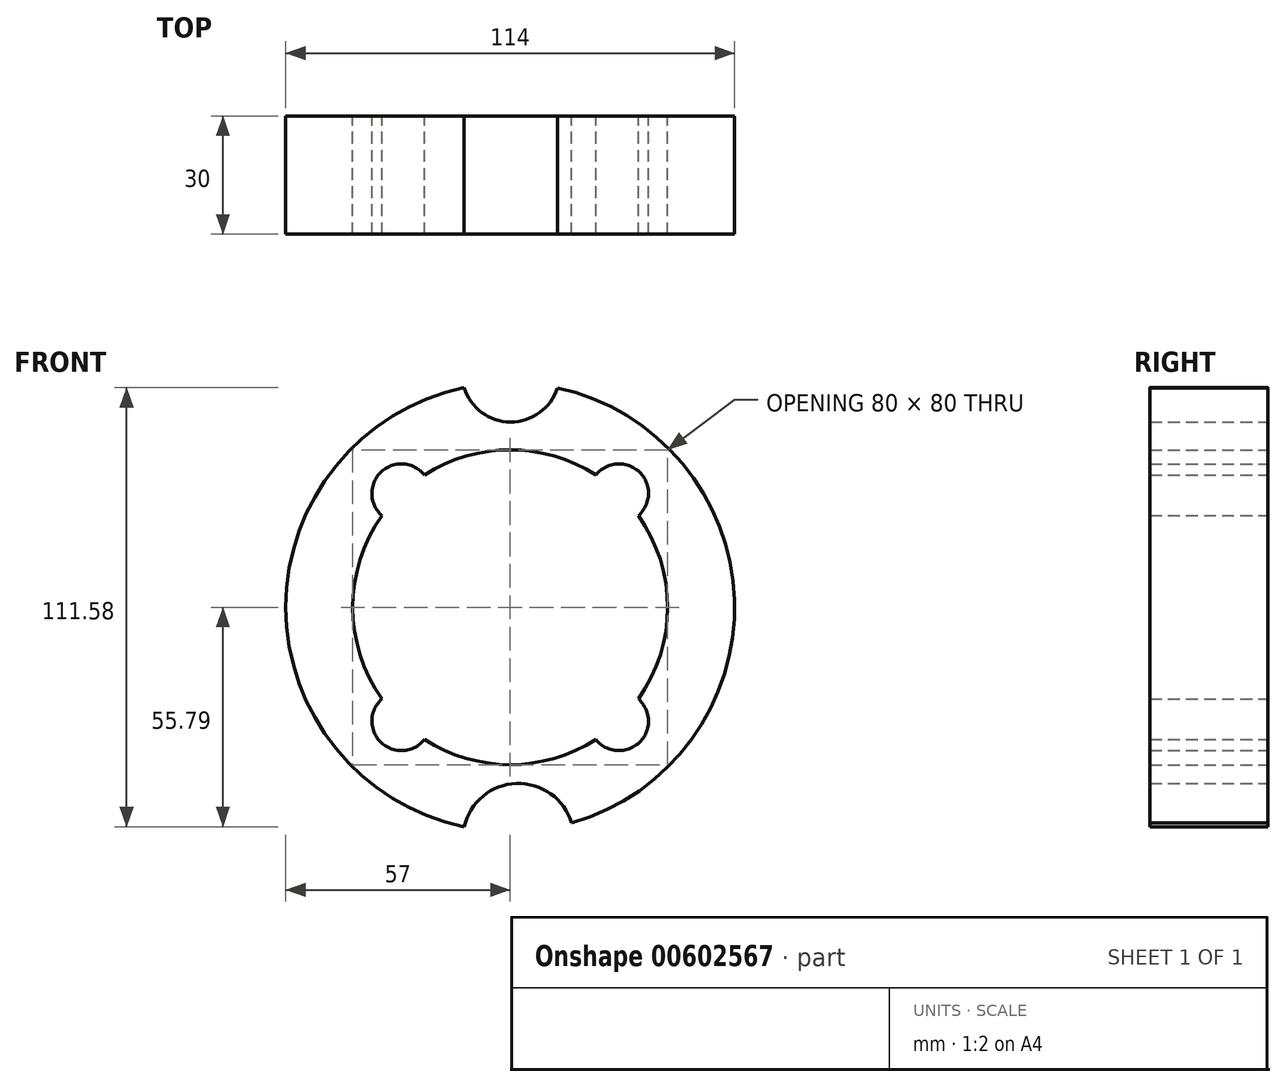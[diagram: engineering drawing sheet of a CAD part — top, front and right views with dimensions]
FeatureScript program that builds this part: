
annotation { "Feature Type Name" : "Feature", "Feature Type Description" : "" }
export const myFeature = defineFeature(function(context is Context, id is Id, definition is map)
    precondition{}
    {
        {
            var Q0;
            Q0=qCreatedBy(makeId("Front.planeOp"),FACE);
            var sketch = newSketch(context, id + "F0", { "sketchPlane" : qUnion([Q0])});
            skArc(sketch, "E0", {"start": v(-11.7, 55.79) * mm, "mid": v(-57, 0) * mm, "end": v(-11.7, -55.79) * mm});
            skCircle(sketch, "E1", {"center": v(0, 0) * mm, "radius": 13 * mm});
            skCircle(sketch, "E2", {"center": v(0, 0) * mm, "radius": 40 * mm});
            skCircle(sketch, "E3", {"center": v(0, 0) * mm, "radius": 25 * mm});
            skArc(sketch, "E4", {"start": v(-11.7, 55.79) * mm, "mid": v(0.12, 47.05) * mm, "end": v(11.98, 55.73) * mm});
            skArc(sketch, "E5", {"start": v(15.62, -54.82) * mm, "mid": v(1.59, -44.78) * mm, "end": v(-11.7, -55.79) * mm});
            skArc(sketch, "E6.trimOffspring", {"start": v(15.62, -54.82) * mm, "mid": v(56.97, 1.88) * mm, "end": v(11.98, 55.73) * mm});
            skCircle(sketch, "E7", {"center": v(-27.64, 28.92) * mm, "radius": 7.5 * mm});
            skCircle(sketch, "E8", {"center": v(27.64, 28.92) * mm, "radius": 7.5 * mm});
            skCircle(sketch, "E9", {"center": v(27.64, -28.92) * mm, "radius": 7.5 * mm});
            skCircle(sketch, "E10", {"center": v(-27.64, -28.92) * mm, "radius": 7.5 * mm});
            skSolve(sketch);
        }
        {
            var Q0;
            Q0 = qSketchRegion(id + "F0", true);
            extrude(context, id + "F1", {"entities" : qUnion([Q0]), "depth" : 30 * mm, "offsetDistance" : 25 * mm});
        }
    });
